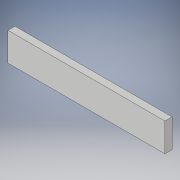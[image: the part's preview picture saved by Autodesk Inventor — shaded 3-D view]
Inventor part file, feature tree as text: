
AUTODESK INVENTOR PART (.ipt)
format: ipt  version: 2017 (Build 210142000, 142)  size: 89,600 bytes
history: native  units: in
note: dims shown in document units (in); Inventor stores cm internally (conversion verified against a paired STEP export)
features: extrude x1, sketch x1
ambient origin geometry x8: Origin, YZ Plane, XZ Plane, XY Plane, X Axis, Y Axis, Z Axis, Center Point
bodies: Solid1 (feature_tree)
feature tree (2):
  extrude  "Extrusion1"  Depth=3.5in
  sketch  "Sketch1"  dims[d0=19.3333in d1=3.5in d2=0.875in d3=0.0in]
